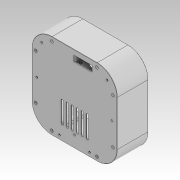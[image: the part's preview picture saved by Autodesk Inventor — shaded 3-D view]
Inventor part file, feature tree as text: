
AUTODESK INVENTOR PART (.ipt)
format: ipt  version: 2020 (Build 240168000, 168)  size: 795,136 bytes
history: native  units: mm
features: sketch x22, extrude x19, projected_geometry x7, other x4, plane x4, chamfer x2, loft x1, fillet x1
ambient origin geometry x8: Origin, YZ Plane, XZ Plane, XY Plane, X Axis, Y Axis, Z Axis, Center Point
bodies: Solid1 (feature_tree)
feature tree (60):
  other  "Blocks"
  sketch  "Sketch1"  dims[d1=170.0mm d2=170.0mm]
  extrude  "Extrusion1"  Depth=170.0mm
  extrude  "Extrusion2"  Depth=62.0mm TaperAngle=0.0deg
  plane  "Work Plane1"
  loft  "Loft1"
  extrude  "Extrusion3"  Depth=7.5mm
  plane  "Work Plane2"
  sketch  "Sketch6"  dims[d14=17.5mm d15=7.5mm]
  plane  "Work Plane3"
  sketch  "Sketch7"  dims[d16=10.0mm d17=65.0mm]
  extrude  "Extrusion4"  Depth=7.5mm
  extrude  "Extrusion5"  Depth=7.5mm
  extrude  "Extrusion7"  Depth=10.0mm
  extrude  "Extrusion8"  Depth=7.5mm
  extrude  "SnipSnip"  TaperAngle=0.0deg  [1 undecoded]
  extrude  "Extrusion10"  Depth=5.0mm TaperAngle=0.0deg
  extrude  "Extrusion11"  [1 undecoded]
  extrude  "Extrusion12"  Depth=2.5mm
  extrude  "Extrusion14"  Depth=10.0mm
  plane  "Work Plane4"
  extrude  "Extrusion15"  Depth=77.0mm TaperAngle=0.0deg
  extrude  "Extrusion16"  Depth=10.0mm
  extrude  "Extrusion17"  Depth=10.0mm TaperAngle=0.0deg
  extrude  "Extrusion18"  TaperAngle=45.0deg  [1 undecoded]
  extrude  "Extrusion19"  Depth=40.0mm TaperAngle=360.0deg
  extrude  "Extrusion20"  TaperAngle=0.0deg  [1 undecoded]
  sketch  "Sketch26"  dims[d72=35.0mm d73=8.0mm d92=55.0mm d93=15.0mm d94=74.1mm d95=52.0mm d96=2.4mm d97=45.0mm d99=6.0mm d100=7.0mm d101=0.0mm d102=26.0mm d103=57.0mm d104=47.0mm d105=28.0mm d106=4.5mm d107=40.0mm d108=5.0mm d109=0.0mm d110=56.2mm d111=60.0deg d112=3.0mm d113=0.0mm d114=3.0mm d115=0.0mm d116=75.0mm d117=92.0mm d118=3.8mm d119=15.0mm d120=0.0mm d121=0.0mm d122=15.0mm d123=7.2mm d124=2.5mm d125=0.0mm d126=32.0mm d127=10.0mm d128=0.0mm d129=35.0mm d131=14.0mm d132=13.0mm d134=12.0mm d135=8.0mm d136=28.0mm d137=0.0mm d139=0.5mm d140=2.0mm d141=45.0deg d142=5.0mm d143=1.0mm d145=0.0mm d146=0.5mm d147=2.0mm d148=45.0deg d149=1.0mm d150=1.0mm d151=14.0mm d152=2.0mm]
  extrude  "Extrusion21"  Depth=21.0mm
  chamfer  "Chamfer1"  Distance=8.0mm
  fillet  "Fillet1"  Radius=55.0mm
  chamfer  "Chamfer2"  Distance=15.0mm
  sketch  "Sketch2"  dims[d3=40.0mm d4=62.0mm d5=0.0mm]
  other  "Block1"
  sketch  "Sketch3"  dims[d7=0.0mm d8=0.0mm d9=5.5mm]
  sketch  "Sketch4"  dims[d10=57.5mm d11=7.5mm]
  projected_geometry  "Projected Loop1"
  sketch  "Sketch5"  dims[d12=7.5mm d13=7.5mm]
  projected_geometry  "Projected Loop2"
  projected_geometry  "Projected Loop3"
  projected_geometry  "Projected Loop4"
  sketch  "Sketch8"  dims[d18=7.5mm d19=7.5mm]
  sketch  "Sketch10"  dims[d20=15.0mm d21=0.0mm d22=90.0deg]
  sketch  "Sketch11"  dims[d23=0.0mm d24=90.0deg d25=5.0mm d26=0.0mm]
  sketch  "Sketch12"  dims[d27=175.0mm d28=-1.5mm]
  sketch  "Sketch13"  dims[d29=2.5mm d30=4.0mm]
  sketch  "Sketch14"  dims[d31=10.0mm d32=0.0mm d33=145.0mm]
  projected_geometry  "Projected Loop5"
  sketch  "Sketch15"  dims[d34=29.75mm d35=0.0mm d41=77.0mm d42=0.0mm]
  sketch  "Sketch18"  dims[d44=2.5mm d45=60.0mm d47=10.0mm d48=10.0mm d50=10.0mm]
  sketch  "Sketch19"  dims[d52=10.0mm d53=0.0mm d54=60.0mm d55=0.0mm]
  sketch  "Sketch20"  dims[d56=10.0mm d57=0.0mm d59=45.0deg]
  projected_geometry  "Projected Loop6"
  sketch  "Sketch21"  dims[d60=5.5mm d61=40.0mm d63=360.0deg]
  sketch  "Sketch22"  dims[d65=10.0mm d66=0.0mm d67=0.0mm d68=0.0mm]
  sketch  "Sketch23"  dims[d69=9.6mm d70=21.0mm]
  sketch  "Sketch24"  dims[d71=1.0mm]
  projected_geometry  "Projected Loop7"
  other  "Block1:1"
  other  "Block1:2"
note: 4 required parameter values undecoded (feature->parameter linkage not recoverable at this tier; creation-order binding heuristic only, values carry confidence <= 0.55)
